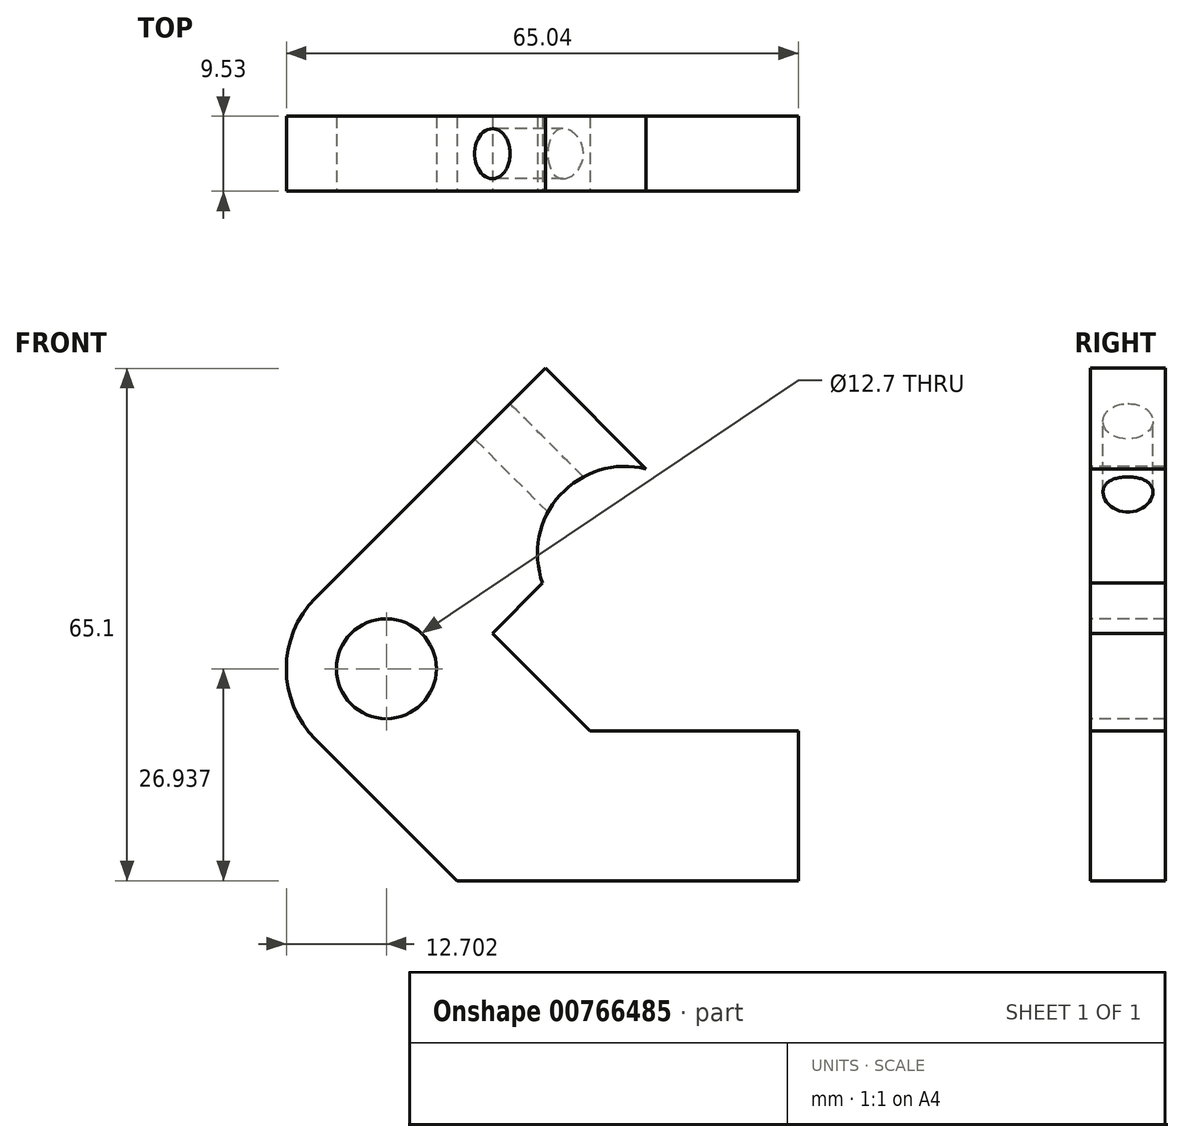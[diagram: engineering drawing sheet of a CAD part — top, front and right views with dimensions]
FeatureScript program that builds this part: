
annotation { "Feature Type Name" : "Feature", "Feature Type Description" : "" }
export const myFeature = defineFeature(function(context is Context, id is Id, definition is map)
    precondition{}
    {
        {
            var Q0;
            Q0=qCreatedBy(makeId("Front.planeOp"),FACE);
            var sketch = newSketch(context, id + "F0", { "sketchPlane" : qUnion([Q0])});
            skArc(sketch, "E0", {"start": v(47.14, 67.93) * mm, "mid": v(36.22, 64.61) * mm, "end": v(33.98, 53.42) * mm});
            skLineSegment(sketch, "E1", {"start": v(44.45, 57.15) * mm, "end": v(18.34, 57.15) * mm, "construction": true});
            skLineSegment(sketch, "E2", {"start": v(44.45, 57.15) * mm, "end": v(36.6, 65) * mm, "construction": true});
            skLineSegment(sketch, "E3.0", {"start": v(47.14, 67.93) * mm, "end": v(34.35, 80.72) * mm});
            skLineSegment(sketch, "E4", {"start": v(36.6, 65) * mm, "end": v(5.16, 33.58) * mm, "construction": true});
            skLineSegment(sketch, "E5.0", {"start": v(18.63, 38.07) * mm, "end": v(9.44, 47.26) * mm, "construction": true});
            skCircle(sketch, "E6", {"center": v(14.14, 42.56) * mm, "radius": 6.35 * mm});
            skLineSegment(sketch, "E7.0", {"start": v(34.35, 80.72) * mm, "end": v(5.16, 51.54) * mm});
            skLineSegment(sketch, "E8.0", {"start": v(40, 34.67) * mm, "end": v(27.61, 47.05) * mm});
            skLineSegment(sketch, "E9.0", {"start": v(23.12, 15.62) * mm, "end": v(5.16, 33.58) * mm});
            skLineSegment(sketch, "E10.0", {"start": v(33.98, 53.42) * mm, "end": v(27.61, 47.05) * mm});
            skLineSegment(sketch, "E11", {"start": v(23.12, 15.62) * mm, "end": v(66.48, 15.62) * mm});
            skLineSegment(sketch, "E12.0", {"start": v(40, 34.67) * mm, "end": v(66.48, 34.67) * mm});
            skLineSegment(sketch, "E13.0", {"start": v(66.48, 15.62) * mm, "end": v(66.48, 34.67) * mm});
            skArc(sketch, "E14.trimOffspring", {"start": v(5.16, 51.54) * mm, "mid": v(1.44, 42.56) * mm, "end": v(5.16, 33.58) * mm});
            skSolve(sketch);
        }
        {
            var Q0;
            Q0=qSketchRegion(id+"F0",true);
            extrude(context, id + "F1", {"entities" : qUnion([Q0]), "oppositeDirection" : true, "depth" : 9.52 * mm, "offsetDistance" : 25.4 * mm});
        }
        {
            var Q0;
            Q0=makeQuery(id+"F1.opExtrude","SWEPT_FACE",FACE,{"disambiguationData":[OSD([sQuery(id+"F0.wireOp",EDGE,"E7.0")])]});
            var sketch = newSketch(context, id + "F2", { "sketchPlane" : qUnion([Q0])});
            skCircle(sketch, "E15", {"center": v(-4.76, 71.84) * mm, "radius": 3.18 * mm});
            skSolve(sketch);
        }
        {
            var Q0;
            Q0=qSketchRegion(id+"F2",true);
            extrude(context, id + "F3", {"entities" : qUnion([Q0]), "operationType" : NewBodyOperationType.REMOVE, "oppositeDirection" : true, "depth" : 25.4 * mm, "offsetDistance" : 25.4 * mm});
        }
    });
